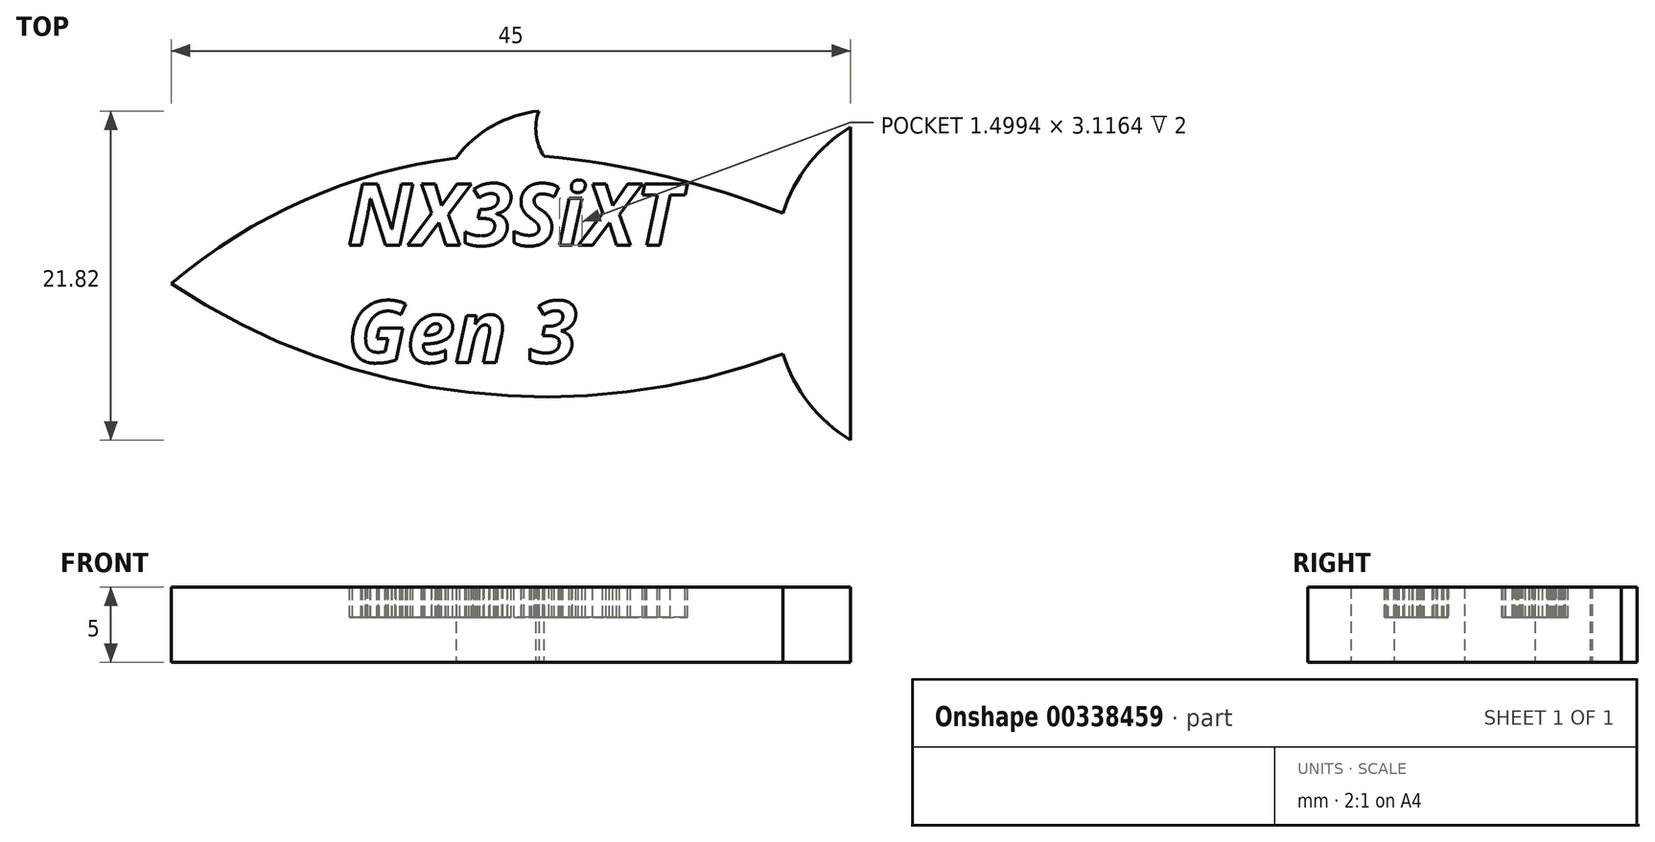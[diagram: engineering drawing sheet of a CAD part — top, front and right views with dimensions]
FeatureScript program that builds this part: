
annotation { "Feature Type Name" : "Feature", "Feature Type Description" : "" }
export const myFeature = defineFeature(function(context is Context, id is Id, definition is map)
    precondition{}
    {
        {
            var Q0;
            Q0=qCreatedBy(makeId("Top.planeOp"),FACE);
            var sketch = newSketch(context, id + "F0", { "sketchPlane" : qUnion([Q0])});
            skArc(sketch, "E0", {"start": v(-1.15, 8.32) * mm, "mid": v(-11.18, 5.53) * mm, "end": v(-20, 0) * mm});
            skArc(sketch, "E1", {"start": v(20.5, 4.66) * mm, "mid": v(12.72, 7.12) * mm, "end": v(4.68, 8.45) * mm});
            skArc(sketch, "E2", {"start": v(25, 10.38) * mm, "mid": v(22.23, 7.93) * mm, "end": v(20.5, 4.66) * mm});
            skLineSegment(sketch, "E3.MirrorCS", {"start": v(4.56, -8.64) * mm, "end": v(4.68, -8.45) * mm});
            skArc(sketch, "E4.MirrorCS", {"start": v(25, -10.38) * mm, "mid": v(22.23, -7.93) * mm, "end": v(20.5, -4.66) * mm});
            skLineSegment(sketch, "E5", {"start": v(25, 10.38) * mm, "end": v(25, -10.38) * mm});
            skPoint(sketch, "E6.MirrorCS.end.orphan", {"position": v(4.68, -8.45) * mm});
            skPoint(sketch, "E7.orphan", {"position": v(3.04, -11.04) * mm});
            skPoint(sketch, "E8.MirrorCS.start.orphan", {"position": v(0, -8.45) * mm});
            skPoint(sketch, "E9.orphan", {"position": v(3.04, 11.04) * mm});
            skLineSegment(sketch, "E10", {"start": v(0, 0) * mm, "end": v(25, 0) * mm});
            skArc(sketch, "E11", {"start": v(-20, 0) * mm, "mid": v(-0.31, -7.22) * mm, "end": v(20.5, -4.66) * mm});
            skPoint(sketch, "E12.end.orphan", {"position": v(20.5, -4.66) * mm});
            skPoint(sketch, "E13.MirrorCS.end.orphan", {"position": v(-20, 0) * mm});
            skArc(sketch, "E14", {"start": v(4.35, 11.44) * mm, "mid": v(4.16, 9.9) * mm, "end": v(4.68, 8.45) * mm});
            skPoint(sketch, "E15.start.orphan", {"position": v(3.04, 11.44) * mm});
            skArc(sketch, "E16", {"start": v(4.35, 11.44) * mm, "mid": v(1.28, 10.45) * mm, "end": v(-1.15, 8.32) * mm});
            skPoint(sketch, "E17.orphan", {"position": v(0, 8.45) * mm});
            skSolve(sketch);
        }
        {
            var Q0;
            Q0 = qSketchRegion(id + "F0", true);
            extrude(context, id + "F1", {"entities" : qUnion([Q0]), "depth" : 5 * mm, "offsetDistance" : 25 * mm});
        }
        {
            var Q0;
            Q0=makeQuery(id+"F1.opExtrude","CAP_FACE",FACE,{"disambiguationData":[OSD([sQuery(id+"F0.wireOp",EDGE,"E0"),sQuery(id+"F0.wireOp",EDGE,"E1"),sQuery(id+"F0.wireOp",EDGE,"E2"),sQuery(id+"F0.wireOp",EDGE,"E4.MirrorCS"),sQuery(id+"F0.wireOp",EDGE,"E5"),sQuery(id+"F0.wireOp",EDGE,"E11"),sQuery(id+"F0.wireOp",EDGE,"E14"),sQuery(id+"F0.wireOp",EDGE,"E16")])],"isStart":false});
            var sketch = newSketch(context, id + "F2", { "sketchPlane" : qUnion([Q0])});
            skText(sketch, "E18", { "text": "NX3SiXT\nGen 3", "fontName": "OpenSans-BoldItalic.ttf"});
            const initialGuessF2  = {"E18": [-0.00834, 0.00253, 1, 0, 0.00411]};
            skSetInitialGuess(sketch, initialGuessF2);
            skSolve(sketch);
        }
        {
            var Q0;
            Q0 = qSketchRegion(id + "F2", true);
            extrude(context, id + "F3", {"entities" : qUnion([Q0]), "operationType" : NewBodyOperationType.REMOVE, "oppositeDirection" : true, "depth" : 2 * mm, "offsetDistance" : 25 * mm});
        }
    });
